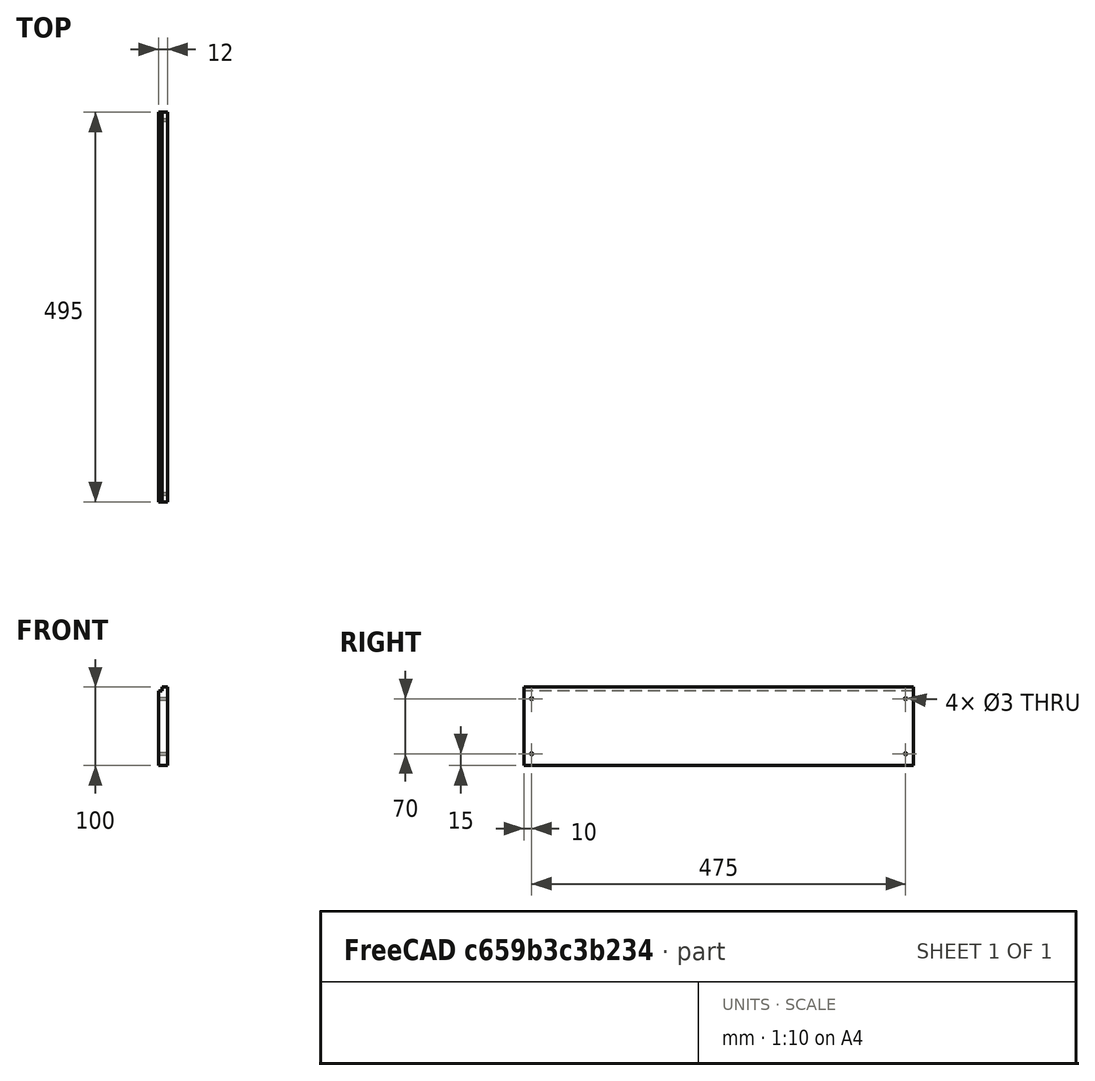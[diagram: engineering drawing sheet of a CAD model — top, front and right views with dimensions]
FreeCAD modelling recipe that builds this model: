
FCSTD DOCUMENT  (FreeCAD 0.20R29177 (Git))
Label: 8000_WindowFrameBottomBack_
License: All rights reserved
LicenseURL: http://en.wikipedia.org/wiki/All_rights_reserved
objects: TechDraw::DrawViewDimension×6, Sketcher::SketchObject×3, PartDesign::Pocket×2, TechDraw::DrawViewPart×2, Spreadsheet::Sheet×1, PartDesign::Pad×1, TechDraw::DrawSVGTemplate×1, PartDesign::Body×1, TechDraw::DrawPage×1
note: 10 computed .brp shape members not serialized (recipe doc carries the construction recipe); baked Part::Feature solids carry a one-line shape summary decoded from their .brp

FEATURE [Sketcher::SketchObject] Sketch
  FullyConstrained = true
  MapMode = 4
  Placement = pos=(0,0,0) rot=(0.57735,0.57735,0.57735;2.0944rad)
  Support = -> [XY_Plane]
  expr: Constraints[5] = Spreadsheet.nZ
  expr: Constraints[6] = Spreadsheet.nY
  sketch-geometry (5):
    g0: LineSegment StartX=0 StartY=0 StartZ=0 EndX=0 EndY=100 EndZ=0
    g1: LineSegment StartX=495 StartY=0 StartZ=0 EndX=495 EndY=100 EndZ=0
    g2: LineSegment StartX=495 StartY=100 StartZ=0 EndX=0 EndY=100 EndZ=0
    g3: LineSegment StartX=247.5 StartY=0 StartZ=0 EndX=0 EndY=0 EndZ=0
    g4: LineSegment StartX=495 StartY=0 StartZ=0 EndX=247.5 EndY=0 EndZ=0
  constraints (14):
    c: Vertical(g0)
    c: Vertical(g1)
    c: Coincident(g2,g1)
    c: Coincident(g2,g0)
    c: Horizontal(g2)
    c: DistanceY(g1,g1) = 100
    c: DistanceX(g2,g2) = 495
    c: Coincident(g3,g0)
    c: Coincident(g4,g1)
    c: Horizontal(g4)
    c: Equal(g3,g4)
    c: Coincident(g4,g3)
    c: Horizontal(g3)
    c: Coincident(g0,g-1)
FEATURE [Spreadsheet::Sheet] Spreadsheet  label="xls"
  cells = B2=BODY FLOOR; E2=Ex.Ref.; B3=Thichness; C3=.T; D3=12; E3=mm; B7=KEYBOARD FRONT; D7=Sperrholz Birke 12 mm; B8=Width; C8=nY; D8(nY)=495; B9=Height; C9=nZ; D9(nZ)=100; E9=F(T); B10=Thickness; C10=nT; D10(nT)=12
FEATURE [PartDesign::Pad] Pad
  AllowMultiFace = false
  Direction = (1,1,1)
  Length = 12
  Length2 = 100
  Profile = -> Sketch
  Reversed = true
  Type = 0
  expr: Length = Spreadsheet.nT
FEATURE [TechDraw::DrawSVGTemplate] Template
  EditableTexts = Designed_by_Name=RIP 2023 09 17; Drawing_number=8000_WindowFrameBottomBack; FC-Date=2024 06 20; FC-SC=0.4; FC-SH=1/1; FC-Title=Window Frame Back Pannel; Subtitle=Stabliizer Strut; Weight=?
  Height = 210
  Orientation = 1
  Width = 297
FEATURE [Sketcher::SketchObject] Sketch001
  ExternalGeometry = -> [Pad]
  FullyConstrained = false
  MapMode = 5
  Placement = pos=(0,0,0) rot=(0.57735,0.57735,0.57735;2.0944rad)
  Support = -> [Pad]
  sketch-geometry (9):
    g0: LineSegment StartX=10 StartY=85 StartZ=0 EndX=485 EndY=85 EndZ=0
    g1: LineSegment StartX=485 StartY=85 StartZ=0 EndX=485 EndY=15 EndZ=0
    g2: LineSegment StartX=485 StartY=15 StartZ=0 EndX=10 EndY=15 EndZ=0
    g3: LineSegment StartX=10 StartY=15 StartZ=0 EndX=10 EndY=85 EndZ=0
    g4: Circle CenterX=10 CenterY=85 CenterZ=0 NormalX=0 NormalY=0 NormalZ=1 AngleXU=0 Radius=1.5
    g5: Circle CenterX=10 CenterY=15 CenterZ=0 NormalX=0 NormalY=0 NormalZ=1 AngleXU=0 Radius=1.5
    g6: Circle CenterX=485 CenterY=15 CenterZ=0 NormalX=0 NormalY=0 NormalZ=1 AngleXU=0 Radius=1.5
    g7: Circle CenterX=485 CenterY=85 CenterZ=0 NormalX=0 NormalY=0 NormalZ=1 AngleXU=0 Radius=1.5
    g8: Circle CenterX=455 CenterY=50 CenterZ=0 NormalX=0 NormalY=0 NormalZ=1 AngleXU=0 Radius=22.5086
  constraints (22):
    c: Coincident(g0,g1)
    c: Coincident(g1,g2)
    c: Coincident(g2,g3)
    c: Coincident(g3,g0)
    c: Horizontal(g0)
    c: Horizontal(g2)
    c: Vertical(g1)
    c: Vertical(g3)
    c: Coincident(g4,g0)
    c: Coincident(g5,g2)
    c: Coincident(g6,g1)
    c: Coincident(g7,g0)
    c: Equal(g4,g5)
    c: Equal(g5,g6)
    c: Equal(g6,g7)
    c: Diameter(g4) = 3
    c: DistanceY(g4,g-3) = 15
    c: DistanceX(g-3,g4) = 10
    c: DistanceY(g-1,g5) = 15
    c: DistanceX(g7,g-3) = 10
    c: DistanceX(g8,g-3) = 40
    c: DistanceY(g8,g-3) = 50
FEATURE [PartDesign::Pocket] Pocket
  BaseFeature = -> Pad
  Direction = (-1,0,0)
  Length = 5
  Length2 = 5
  Profile = -> Sketch001
  ReferenceAxis = -> Sketch001 [N_Axis]
  Type = 1
  UseCustomVector = true
FEATURE [TechDraw::DrawViewPart] View
  CoarseView = false
  Direction = (1,0,0)
  Focus = 100
  HardHidden = false
  IsoCount = 0
  IsoHidden = false
  IsoVisible = false
  LockPosition = false
  Perspective = false
  Rotation = 0
  Scale = 0.4
  ScaleType = 2
  SeamHidden = false
  SeamVisible = true
  SmoothHidden = false
  SmoothVisible = true
  Source = -> [Pocket]
  X = 115.847
  XDirection = (0,1,0)
  Y = 140.969
FEATURE [TechDraw::DrawViewDimension] Dimension
  AngleOverride = false
  Arbitrary = false
  ArbitraryTolerances = false
  EqualTolerance = true
  ExtensionAngle = 0
  FormatSpec = %.2f
  FormatSpecOverTolerance = %+.2f
  FormatSpecUnderTolerance = %+.2f
  Inverted = false
  LineAngle = 0
  LockPosition = false
  MeasureType = 1
  OverTolerance = 0
  References2D = -> [View]
  Rotation = 0
  ScaleType = 0
  TheoreticalExact = false
  Type = 1
  UnderTolerance = 0
  X = 4.3299
  Y = 34.768
FEATURE [TechDraw::DrawViewDimension] Dimension001
  AngleOverride = false
  Arbitrary = false
  ArbitraryTolerances = false
  EqualTolerance = true
  ExtensionAngle = 0
  FormatSpec = %.2f
  FormatSpecOverTolerance = %+.2f
  FormatSpecUnderTolerance = %+.2f
  Inverted = false
  LineAngle = 0
  LockPosition = false
  MeasureType = 1
  OverTolerance = 0
  References2D = -> [View]
  Rotation = 0
  ScaleType = 0
  TheoreticalExact = false
  Type = 2
  UnderTolerance = 0
  X = 7.752
  Y = 0.464249
FEATURE [TechDraw::DrawViewDimension] Dimension004
  AngleOverride = false
  Arbitrary = false
  ArbitraryTolerances = false
  EqualTolerance = true
  ExtensionAngle = 0
  FormatSpec = ⌀%.2f
  FormatSpecOverTolerance = %+.2f
  FormatSpecUnderTolerance = %+.2f
  Inverted = false
  LineAngle = 0
  LockPosition = false
  MeasureType = 1
  OverTolerance = 0
  References2D = -> [View]
  Rotation = 0
  ScaleType = 0
  TheoreticalExact = false
  Type = 5
  UnderTolerance = 0
  X = 77.2994
  Y = -1.86277
FEATURE [Sketcher::SketchObject] Sketch002
  ExternalGeometry = -> [Pocket]
  FullyConstrained = true
  MapMode = 5
  Placement = pos=(0,495,0) rot=(0,0.707107,0.707107;3.14159rad)
  Support = -> [Pocket]
  sketch-geometry (4):
    g0: LineSegment StartX=12 StartY=100 StartZ=0 EndX=7 EndY=100 EndZ=0
    g1: LineSegment StartX=7 StartY=100 StartZ=0 EndX=7 EndY=95 EndZ=0
    g2: LineSegment StartX=7 StartY=95 StartZ=0 EndX=12 EndY=95 EndZ=0
    g3: LineSegment StartX=12 StartY=95 StartZ=0 EndX=12 EndY=100 EndZ=0
  constraints (11):
    c: Coincident(g0,g1)
    c: Coincident(g1,g2)
    c: Coincident(g2,g3)
    c: Coincident(g3,g0)
    c: Horizontal(g0)
    c: Horizontal(g2)
    c: Vertical(g1)
    c: Vertical(g3)
    c: Coincident(g0,g-4)
    c: DistanceX(g0,g0) = 5
    c: DistanceY(g3,g3) = 5
FEATURE [PartDesign::Pocket] Pocket001
  BaseFeature = -> Pocket
  Direction = (0,-1,2e-16)
  Length = 5
  Length2 = 5
  Profile = -> Sketch002
  ReferenceAxis = -> Sketch002 [N_Axis]
  Type = 1
FEATURE [PartDesign::Body] Body
  Group = -> [Sketch,Pad,Sketch001,Pocket,Sketch002,Pocket001]
  Origin = -> Origin
  Tip = -> Pocket001
FEATURE [TechDraw::DrawViewPart] View002
  CoarseView = false
  Direction = (0,1,0)
  Focus = 100
  HardHidden = false
  IsoCount = 0
  IsoHidden = false
  IsoVisible = false
  LockPosition = false
  Perspective = false
  Rotation = 0
  Scale = 0.5
  ScaleType = 2
  SeamHidden = false
  SeamVisible = true
  SmoothHidden = false
  SmoothVisible = true
  Source = -> [Pocket001]
  X = 268.628
  XDirection = (1,0,0)
  Y = 137.953
FEATURE [TechDraw::DrawViewDimension] Dimension005
  AngleOverride = false
  Arbitrary = false
  ArbitraryTolerances = false
  EqualTolerance = true
  ExtensionAngle = 0
  FormatSpec = %.2f
  FormatSpecOverTolerance = %+.2f
  FormatSpecUnderTolerance = %+.2f
  Inverted = false
  LineAngle = 0
  LockPosition = false
  MeasureType = 1
  OverTolerance = 0
  References2D = -> [View002]
  Rotation = 0
  ScaleType = 0
  TheoreticalExact = false
  Type = 2
  UnderTolerance = 0
  X = -20.3739
  Y = -12.9158
FEATURE [TechDraw::DrawViewDimension] Dimension006
  AngleOverride = false
  Arbitrary = false
  ArbitraryTolerances = false
  EqualTolerance = true
  ExtensionAngle = 0
  FormatSpec = %.2f
  FormatSpecOverTolerance = %+.2f
  FormatSpecUnderTolerance = %+.2f
  Inverted = false
  LineAngle = 0
  LockPosition = false
  MeasureType = 1
  OverTolerance = 0
  References2D = -> [View002]
  Rotation = 0
  ScaleType = 0
  TheoreticalExact = false
  Type = 1
  UnderTolerance = 0
  X = -14.1139
  Y = -39.9333
FEATURE [TechDraw::DrawViewDimension] Dimension007
  AngleOverride = false
  Arbitrary = false
  ArbitraryTolerances = false
  EqualTolerance = true
  ExtensionAngle = 0
  FormatSpec = %.2f
  FormatSpecOverTolerance = %+.2f
  FormatSpecUnderTolerance = %+.2f
  Inverted = false
  LineAngle = 0
  LockPosition = false
  MeasureType = 1
  OverTolerance = 0
  References2D = -> [View002]
  Rotation = 0
  ScaleType = 0
  TheoreticalExact = false
  Type = 1
  UnderTolerance = 0
  X = -20.3413
  Y = 38.1907
FEATURE [TechDraw::DrawPage] Page
  KeepUpdated = true
  NextBalloonIndex = 1
  ProjectionType = 0
  Template = -> Template
  Views = -> [View,Dimension,Dimension001,Dimension004,View002,Dimension005,Dimension006,Dimension007]
